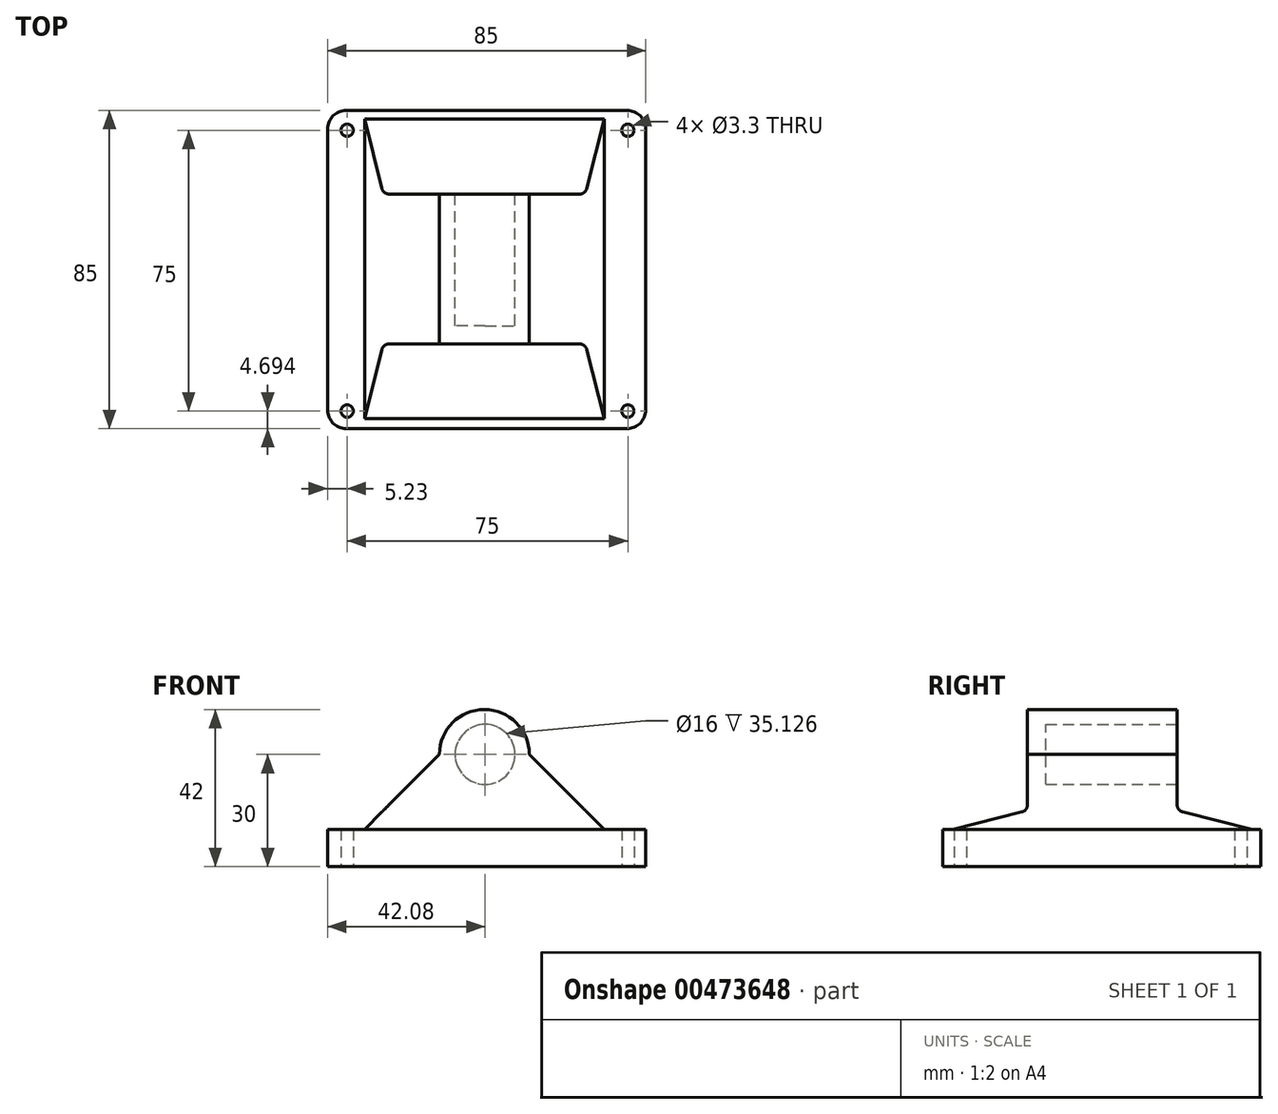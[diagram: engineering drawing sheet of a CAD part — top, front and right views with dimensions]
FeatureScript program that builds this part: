
annotation { "Feature Type Name" : "Feature", "Feature Type Description" : "" }
export const myFeature = defineFeature(function(context is Context, id is Id, definition is map)
    precondition{}
    {
        {
            var Q0;
            Q0=qCreatedBy(makeId("Top.planeOp"),FACE);
            var sketch = newSketch(context, id + "F0", { "sketchPlane" : qUnion([Q0])});
            skLineSegment(sketch, "E0.bottom", {"start": v(-42.08, 42.5) * mm, "end": v(42.92, 42.5) * mm});
            skLineSegment(sketch, "E0.top", {"start": v(-42.08, -42.5) * mm, "end": v(42.92, -42.5) * mm});
            skLineSegment(sketch, "E0.left", {"start": v(-42.08, 42.5) * mm, "end": v(-42.08, -42.5) * mm});
            skLineSegment(sketch, "E0.right", {"start": v(42.92, 42.5) * mm, "end": v(42.92, -42.5) * mm});
            skLineSegment(sketch, "E1", {"start": v(-36.85, 42.5) * mm, "end": v(-36.85, -42.5) * mm, "construction": true});
            skLineSegment(sketch, "E2", {"start": v(38.15, 42.5) * mm, "end": v(38.15, -42.5) * mm, "construction": true});
            skLineSegment(sketch, "E3", {"start": v(-42.08, 37.18) * mm, "end": v(42.92, 37.18) * mm, "construction": true});
            skLineSegment(sketch, "E4", {"start": v(-42.08, -37.82) * mm, "end": v(42.92, -37.82) * mm, "construction": true});
            skCircle(sketch, "E5", {"center": v(-36.85, 37.18) * mm, "radius": 1.65 * mm});
            skCircle(sketch, "E6", {"center": v(38.15, 37.18) * mm, "radius": 1.65 * mm});
            skCircle(sketch, "E7", {"center": v(38.15, -37.82) * mm, "radius": 1.65 * mm});
            skCircle(sketch, "E8", {"center": v(-36.85, -37.82) * mm, "radius": 1.65 * mm});
            skLineSegment(sketch, "E9.bottom", {"start": v(-12.2, 20.13) * mm, "end": v(11.8, 20.13) * mm});
            skLineSegment(sketch, "E9.top", {"start": v(-12.2, -19.87) * mm, "end": v(11.8, -19.87) * mm});
            skLineSegment(sketch, "E9.left", {"start": v(-12.2, 20.13) * mm, "end": v(-12.2, -19.87) * mm});
            skLineSegment(sketch, "E9.right", {"start": v(11.8, 20.13) * mm, "end": v(11.8, -19.87) * mm});
            skLineSegment(sketch, "E10", {"start": v(-12.2, -11.87) * mm, "end": v(11.8, -11.87) * mm});
            skSolve(sketch);
        }
        {
            var Q0;
            Q0=makeQuery(id+"F0.imprint","IMPRINT",FACE,{"disambiguationData":[TD([[makeQuery(id+"F0.imprint","IMPRINT",EDGE,{"derivedFrom":sQuery(id+"F0.wireOp",EDGE,"E0.bottom")}),-1.0]])]});
            var Q1;
            {var subQ0=sQuery(id+"F0.wireOp",EDGE,"E9.bottom");Q1=makeQuery(id+"F0.imprint","IMPRINT",FACE,{"disambiguationData":[TD([[makeQuery(id+"F0.imprint","IMPRINT",EDGE,{"derivedFrom":subQ0}),-1.0]])]});}
            var Q2;
            {var subQ0=sQuery(id+"F0.wireOp",EDGE,"E9.top");Q2=makeQuery(id+"F0.imprint","IMPRINT",FACE,{"disambiguationData":[TD([[makeQuery(id+"F0.imprint","IMPRINT",EDGE,{"derivedFrom":subQ0}),1.0]])]});}
            extrude(context, id + "F1", {"entities" : qUnion([Q0, Q1, Q2]), "depth" : 10 * mm});
        }
        {
            var Q0;
            {var subQ0=sQuery(id+"F0.wireOp",EDGE,"E9.bottom");Q0=makeQuery(id+"F0.imprint","IMPRINT",FACE,{"disambiguationData":[TD([[makeQuery(id+"F0.imprint","IMPRINT",EDGE,{"derivedFrom":subQ0}),-1.0]])]});}
            var Q1;
            {var subQ0=sQuery(id+"F0.wireOp",EDGE,"E9.top");Q1=makeQuery(id+"F0.imprint","IMPRINT",FACE,{"disambiguationData":[TD([[makeQuery(id+"F0.imprint","IMPRINT",EDGE,{"derivedFrom":subQ0}),1.0]])]});}
            extrude(context, id + "F2", {"entities" : qUnion([Q0, Q1]), "operationType" : NewBodyOperationType.ADD, "depth" : 42 * mm});
        }
        {
            var Q0;
            Q0=makeQuery(id+"F1.opExtrude","SWEPT_EDGE",EDGE,{"disambiguationData":[OSD([sQuery(id+"F0.wireOp",EDGE,"E0.bottom"),sQuery(id+"F0.wireOp",EDGE,"E0.left")])]});
            var Q1;
            Q1=makeQuery(id+"F1.opExtrude","SWEPT_EDGE",EDGE,{"disambiguationData":[OSD([sQuery(id+"F0.wireOp",EDGE,"E0.bottom"),sQuery(id+"F0.wireOp",EDGE,"E0.right")])]});
            var Q2;
            Q2=makeQuery(id+"F1.opExtrude","SWEPT_EDGE",EDGE,{"disambiguationData":[OSD([sQuery(id+"F0.wireOp",EDGE,"E0.top"),sQuery(id+"F0.wireOp",EDGE,"E0.left")])]});
            var Q3;
            Q3=makeQuery(id+"F1.opExtrude","SWEPT_EDGE",EDGE,{"disambiguationData":[OSD([sQuery(id+"F0.wireOp",EDGE,"E0.top"),sQuery(id+"F0.wireOp",EDGE,"E0.right")])]});
            fillet(context, id + "F3", {"entities" : qUnion([Q0, Q1, Q2, Q3]), "radius" : 5 * mm, "tangentPropagation" : true, "allowEdgeOverflow" : false});
        }
        {
            var Q0;
            Q0=makeQuery(id+"F2.opExtrude","CAP_EDGE",EDGE,{"disambiguationData":[OSD([sQuery(id+"F0.wireOp",EDGE,"E9.left")])],"isStart":false});
            var Q1;
            Q1=makeQuery(id+"F2.opExtrude","CAP_EDGE",EDGE,{"disambiguationData":[OSD([sQuery(id+"F0.wireOp",EDGE,"E9.right")])],"isStart":false});
            fillet(context, id + "F4", {"entities" : qUnion([Q0, Q1]), "radius" : 12 * mm, "tangentPropagation" : true, "allowEdgeOverflow" : false});
        }
        {
            var Q0;
            Q0=makeQuery(id+"F2.boolean.opBoolean","INTERSECT",EDGE,{"derivedFrom":[makeQuery(id+"F1.opExtrude","CAP_FACE",FACE,{"disambiguationData":[OSD([sQuery(id+"F0.wireOp",EDGE,"E0.bottom"),sQuery(id+"F0.wireOp",EDGE,"E0.top"),sQuery(id+"F0.wireOp",EDGE,"E0.left"),sQuery(id+"F0.wireOp",EDGE,"E0.right"),sQuery(id+"F0.wireOp",EDGE,"E5"),sQuery(id+"F0.wireOp",EDGE,"E6"),sQuery(id+"F0.wireOp",EDGE,"E7"),sQuery(id+"F0.wireOp",EDGE,"E8")])],"isStart":false}),makeQuery(id+"F2.opExtrude","SWEPT_FACE",FACE,{"disambiguationData":[OSD([sQuery(id+"F0.wireOp",EDGE,"E9.bottom")])]})]});
            var Q1;
            Q1=makeQuery(id+"F2.boolean.opBoolean","INTERSECT",EDGE,{"derivedFrom":[makeQuery(id+"F1.opExtrude","CAP_FACE",FACE,{"disambiguationData":[OSD([sQuery(id+"F0.wireOp",EDGE,"E0.bottom"),sQuery(id+"F0.wireOp",EDGE,"E0.top"),sQuery(id+"F0.wireOp",EDGE,"E0.left"),sQuery(id+"F0.wireOp",EDGE,"E0.right"),sQuery(id+"F0.wireOp",EDGE,"E5"),sQuery(id+"F0.wireOp",EDGE,"E6"),sQuery(id+"F0.wireOp",EDGE,"E7"),sQuery(id+"F0.wireOp",EDGE,"E8")])],"isStart":false}),makeQuery(id+"F2.opExtrude","SWEPT_FACE",FACE,{"disambiguationData":[OSD([sQuery(id+"F0.wireOp",EDGE,"E9.top")])]})]});
            chamfer(context, id + "F5", {"entities" : qUnion([Q0, Q1]), "chamferType" : ChamferType.TWO_OFFSETS, "width1" : 5 * mm, "oppositeDirection" : false, "width2" : 20 * mm, "tangentPropagation" : true});
        }
        {
            var Q0;
            Q0=qCreatedBy(makeId("Front.planeOp"),FACE);
            var sketch = newSketch(context, id + "F6", { "sketchPlane" : qUnion([Q0])});
            skCircle(sketch, "E11", {"center": v(0, 30) * mm, "radius": 8 * mm});
            skSolve(sketch);
        }
        {
            var Q0;
            Q0=makeQuery(id+"F6.imprint","IMPRINT",FACE,{"disambiguationData":[TD([[makeQuery(id+"F6.imprint","IMPRINT",EDGE,{"derivedFrom":sQuery(id+"F6.wireOp",EDGE,"E11")}),1.0]])]});
            extrude(context, id + "F7", {"entities" : qUnion([Q0]), "operationType" : NewBodyOperationType.REMOVE, "depth" : 15 * mm, "hasSecondDirection" : true, "secondDirectionOppositeDirection" : true, "secondDirectionDepth" : 25 * mm});
        }
        {
            var Q0;
            {var subQ0=makeQuery(id+"F2.opExtrude","SWEPT_FACE",FACE,{"disambiguationData":[OSD([sQuery(id+"F0.wireOp",EDGE,"E9.top")])]});Q0=makeQuery(id+"F5.opChamfer","BLEND_EDGE",EDGE,{"blendedFrom":[makeQuery(id+"F2.boolean.opBoolean","INTERSECT",EDGE,{"derivedFrom":[makeQuery(id+"F1.opExtrude","CAP_FACE",FACE,{"disambiguationData":[OSD([sQuery(id+"F0.wireOp",EDGE,"E0.bottom"),sQuery(id+"F0.wireOp",EDGE,"E0.top"),sQuery(id+"F0.wireOp",EDGE,"E0.left"),sQuery(id+"F0.wireOp",EDGE,"E0.right"),sQuery(id+"F0.wireOp",EDGE,"E5"),sQuery(id+"F0.wireOp",EDGE,"E6"),sQuery(id+"F0.wireOp",EDGE,"E7"),sQuery(id+"F0.wireOp",EDGE,"E8")])],"isStart":false}),subQ0]}),subQ0],"blendedInto":[subQ0]});}
            var Q1;
            {var subQ0=makeQuery(id+"F2.opExtrude","SWEPT_FACE",FACE,{"disambiguationData":[OSD([sQuery(id+"F0.wireOp",EDGE,"E9.bottom")])]});Q1=makeQuery(id+"F5.opChamfer","BLEND_EDGE",EDGE,{"blendedFrom":[makeQuery(id+"F2.boolean.opBoolean","INTERSECT",EDGE,{"derivedFrom":[makeQuery(id+"F1.opExtrude","CAP_FACE",FACE,{"disambiguationData":[OSD([sQuery(id+"F0.wireOp",EDGE,"E0.bottom"),sQuery(id+"F0.wireOp",EDGE,"E0.top"),sQuery(id+"F0.wireOp",EDGE,"E0.left"),sQuery(id+"F0.wireOp",EDGE,"E0.right"),sQuery(id+"F0.wireOp",EDGE,"E5"),sQuery(id+"F0.wireOp",EDGE,"E6"),sQuery(id+"F0.wireOp",EDGE,"E7"),sQuery(id+"F0.wireOp",EDGE,"E8")])],"isStart":false}),subQ0]}),subQ0],"blendedInto":[subQ0]});}
            fillet(context, id + "F8", {"entities" : qUnion([Q0, Q1]), "radius" : 2 * mm, "tangentPropagation" : true, "allowEdgeOverflow" : false});
        }
        {
            var Q0;
            Q0=makeQuery(id+"F2.boolean.opBoolean","INTERSECT",EDGE,{"derivedFrom":[makeQuery(id+"F1.opExtrude","CAP_FACE",FACE,{"disambiguationData":[OSD([sQuery(id+"F0.wireOp",EDGE,"E0.bottom"),sQuery(id+"F0.wireOp",EDGE,"E0.top"),sQuery(id+"F0.wireOp",EDGE,"E0.left"),sQuery(id+"F0.wireOp",EDGE,"E0.right"),sQuery(id+"F0.wireOp",EDGE,"E5"),sQuery(id+"F0.wireOp",EDGE,"E6"),sQuery(id+"F0.wireOp",EDGE,"E7"),sQuery(id+"F0.wireOp",EDGE,"E8")])],"isStart":false}),makeQuery(id+"F2.opExtrude","SWEPT_FACE",FACE,{"disambiguationData":[OSD([sQuery(id+"F0.wireOp",EDGE,"E9.left")])]})]});
            var Q1;
            Q1=makeQuery(id+"F2.boolean.opBoolean","INTERSECT",EDGE,{"derivedFrom":[makeQuery(id+"F1.opExtrude","CAP_FACE",FACE,{"disambiguationData":[OSD([sQuery(id+"F0.wireOp",EDGE,"E0.bottom"),sQuery(id+"F0.wireOp",EDGE,"E0.top"),sQuery(id+"F0.wireOp",EDGE,"E0.left"),sQuery(id+"F0.wireOp",EDGE,"E0.right"),sQuery(id+"F0.wireOp",EDGE,"E5"),sQuery(id+"F0.wireOp",EDGE,"E6"),sQuery(id+"F0.wireOp",EDGE,"E7"),sQuery(id+"F0.wireOp",EDGE,"E8")])],"isStart":false}),makeQuery(id+"F2.opExtrude","SWEPT_FACE",FACE,{"disambiguationData":[OSD([sQuery(id+"F0.wireOp",EDGE,"E9.right")])]})]});
            chamfer(context, id + "F9", {"entities" : qUnion([Q0, Q1]), "chamferType" : ChamferType.TWO_OFFSETS, "width1" : 20 * mm, "oppositeDirection" : false, "width2" : 20 * mm, "tangentPropagation" : true});
        }
    });
